# Revit family: Plumbing_Drainage_hansgrohe_58131XXX-Exafill-Finish-set-chrome-bath-filler
name_source: partatom
category: Plumbing Fixtures
units: mm (PartAtom-declared; Revit-internal decimal feet)

## family parameters
Cut with Voids When Loaded = Yes
Host = Face
Maintain Annotation Orientation = No
OmniClass Number = 23.31.15.17
OmniClass Title = Bathtub Components
Part Type = Normal
Room Calculation Point = No
Round Connector Dimension = Use Diameter
Shared = No

## types (1)
- 58131XXX Exafill Finish set chrome bath filler waste and overflow set
    Default Elevation = 1219 mm
    Description = Exafill Finish set chrome bath filler, waste and overflow set
    Manufacturer = Hansgrohe
    Material 1 = Hansgrohe - Metal - 000 Chrome
    Material 2 = Hansgrohe - Plastic - Black
    Material 3 = Hansgrohe - Metal - High Gloss White
    Model = 58131XXX
    Product Page URL = https://www.hansgrohe.com
    Product data url = https://bimobject.com
    URL = https://www.hansgrohe.com
    Version = 1

## geometry (parser evidence)
native form markers: Sweep x1
no freeform markers — native parametric forms only
